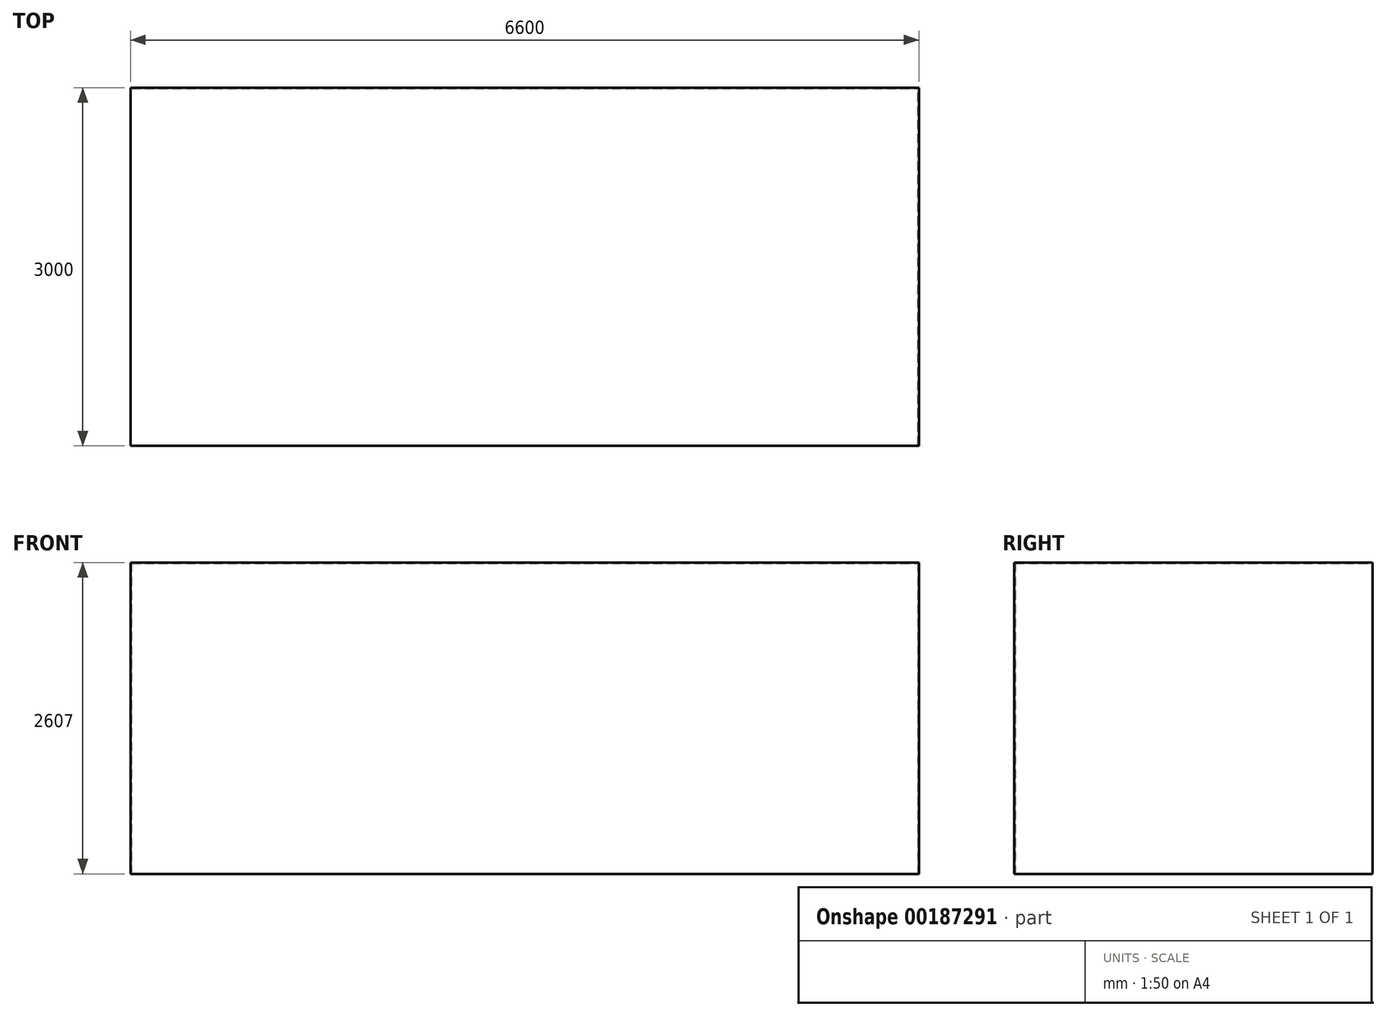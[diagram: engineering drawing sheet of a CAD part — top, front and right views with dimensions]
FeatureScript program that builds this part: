
annotation { "Feature Type Name" : "Feature", "Feature Type Description" : "" }
export const myFeature = defineFeature(function(context is Context, id is Id, definition is map)
    precondition{}
    {
        {
            var Q0;
            Q0=qCreatedBy(makeId("Top.planeOp"),FACE);
            var sketch = newSketch(context, id + "F0", { "sketchPlane" : qUnion([Q0])});
            skLineSegment(sketch, "E0.bottom", {"start": v(0, 0) * mm, "end": v(6600, 0) * mm});
            skLineSegment(sketch, "E0.top", {"start": v(0, 3000) * mm, "end": v(6600, 3000) * mm});
            skLineSegment(sketch, "E0.left", {"start": v(0, 0) * mm, "end": v(0, 3000) * mm});
            skLineSegment(sketch, "E0.right", {"start": v(6600, 0) * mm, "end": v(6600, 3000) * mm});
            skLineSegment(sketch, "E1.0", {"start": v(7, 2993) * mm, "end": v(6593, 2993) * mm});
            skLineSegment(sketch, "E1.1", {"start": v(7, 7) * mm, "end": v(7, 2993) * mm});
            skLineSegment(sketch, "E1.2", {"start": v(7, 7) * mm, "end": v(6593, 7) * mm});
            skLineSegment(sketch, "E1.3", {"start": v(6593, 7) * mm, "end": v(6593, 2993) * mm});
            skSolve(sketch);
        }
        {
            var Q0;
            Q0=makeQuery(id+"F0.imprint","IMPRINT",FACE,{"disambiguationData":[TD([[makeQuery(id+"F0.imprint","IMPRINT",EDGE,{"derivedFrom":sQuery(id+"F0.wireOp",EDGE,"E0.bottom")}),1.0]])]});
            extrude(context, id + "F1", {"entities" : qUnion([Q0]), "depth" : 2600 * mm});
        }
        {
            var Q0;
            Q0=makeQuery(id+"F1.opExtrude","CAP_FACE",FACE,{"disambiguationData":[OSD([sQuery(id+"F0.wireOp",EDGE,"E0.bottom"),sQuery(id+"F0.wireOp",EDGE,"E0.top"),sQuery(id+"F0.wireOp",EDGE,"E0.left"),sQuery(id+"F0.wireOp",EDGE,"E0.right"),sQuery(id+"F0.wireOp",EDGE,"E1.0"),sQuery(id+"F0.wireOp",EDGE,"E1.1"),sQuery(id+"F0.wireOp",EDGE,"E1.2"),sQuery(id+"F0.wireOp",EDGE,"E1.3")])],"isStart":false});
            var sketch = newSketch(context, id + "F2", { "sketchPlane" : qUnion([Q0])});
            skLineSegment(sketch, "E2.0", {"start": v(0, 3000) * mm, "end": v(6600, 3000) * mm});
            skLineSegment(sketch, "E3.0", {"start": v(6600, 0) * mm, "end": v(6600, 3000) * mm});
            skLineSegment(sketch, "E4.0", {"start": v(0, 0) * mm, "end": v(6600, 0) * mm});
            skLineSegment(sketch, "E5.0", {"start": v(0, 0) * mm, "end": v(0, 3000) * mm});
            skSolve(sketch);
        }
        {
            var Q0;
            Q0 = qSketchRegion(id + "F2", true);
            extrude(context, id + "F3", {"entities" : qUnion([Q0]), "operationType" : NewBodyOperationType.ADD, "depth" : 7 * mm});
        }
    });
